# Revit family: Basin-Undercounter-American_Standard-Boxe-0315.000_Series
name_source: partatom
category: Plumbing Fixtures
revit_build: Autodesk Revit 2018 (Build: 20170223_1515(x64)
units: mm (PartAtom-declared; Revit-internal decimal feet)

## family parameters
Always vertical = No
Cut with Voids When Loaded = Yes
OmniClass Number = 23.45.05.14.14
OmniClass Title = Sinks/Lavatories
Part Type = Normal
Room Calculation Point = No
Round Connector Dimension = Use Radius
Shared = Yes
Work Plane-Based = Yes

## types (1)
- 0315000.020
    4" Inlet Connection Width = Yes
    8" Inlet Connection Width = No
    ADA Compliant = Yes
    Assembly Code = D2010310
    Basin Shape = Rectangular
    CW Connection = Yes
    CWFU = 1.5
    Cold Water Connection Diameter = 3/8"
    Cold Water Connection Radius = 3/16"
    Cold Water Connection Width = 2"
    Compliance Certifications = Meets or exceeds ASME A112.19.2M for Vitreous China Fixtures. CAN/CSA B45 Series.
    Counter Opening Length = 12 3/4"
    Counter Opening Width = 16 3/4"
    Default Elevation = 34"
    Description = Boxe® Under Counter Sink
    Finish = Vitreous China-American Standard-020-White
    HW Connection = Yes
    HWFU = 1.5
    Height = 7"
    Hot Water Connection Diameter = 3/8"
    Hot Water Connection Radius = 3/16"
    Hot Water Connection Width = 2"
    Installation Type = Undermount
    Length = 16"
    Manufacturer = American Standard
    Material = Vitreous China-American Standard-020-White
    Model = 0315000.020
    Outlet Width from Wall = 12"
    Price = Prices may vary. Please consult McGuire rep for most up to date price list.
    Product Documentation Link = https://americanstandard.box.com
    Product Page URL = https://www.americanstandard.ca
    Revised Date = 03/14/2022
    Rim Material = Metal-American Standard-Unglazed
    URL = http://www.americanstandard.ca
    Vent Connection = No
    WFU = 2
    Waste Connection = Yes
    Waste Connection Diameter = 1 1/4"
    Waste Connection Radius = 5/8"
    Width = 20"

## geometry (parser evidence)
native form markers: Sweep x2
no freeform markers — native parametric forms only
